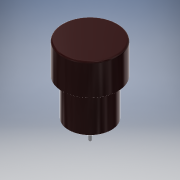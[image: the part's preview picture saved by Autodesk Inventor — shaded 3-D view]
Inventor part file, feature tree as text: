
AUTODESK INVENTOR PART (.ipt)
format: ipt  version: 2019 (Build 230136000, 136)  size: 242,688 bytes
history: native  units: mm
features: fillet x8, extrude x7, sketch x7
ambient origin geometry x8: Origin, YZ Plane, XZ Plane, XY Plane, X Axis, Y Axis, Z Axis, Center Point
bodies: Solid1 (feature_tree)
feature tree (22):
  extrude  "Extrusion1"  Depth=44.0mm TaperAngle=0.0deg
  extrude  "Extrusion2"  Depth=34.0mm TaperAngle=0.0deg
  extrude  "Extrusion3"  Depth=4.0mm TaperAngle=0.0deg
  fillet  "Fillet1"  Radius=2.0mm
  fillet  "Fillet2"  Radius=2.0mm
  fillet  "Fillet4"  Radius=2.0mm
  fillet  "Fillet5"  Radius=0.5mm
  extrude  "Extrusion7"  Depth=3.0mm
  extrude  "Extrusion8"  Depth=3.0mm
  extrude  "Extrusion9"  Depth=2.0mm
  extrude  "Extrusion10"  Depth=0.1mm
  fillet  "Fillet8"  Radius=0.2mm
  fillet  "Fillet9"  Radius=1.0mm
  fillet  "Fillet10"  Radius=0.1mm
  fillet  "Fillet11"  [1 undecoded]
  sketch  "Sketch1"  dims[d0=46.0mm d1=44.0mm d2=0.0mm]
  sketch  "Sketch2"  dims[d3=60.0mm d4=34.0mm d5=0.0mm]
  sketch  "Sketch3"  dims[d6=2.0mm d7=4.0mm d8=0.0mm d9=2.0mm d10=2.0mm d12=2.0mm d13=0.5mm]
  sketch  "Sketch8"  dims[d25=3.0mm d26=0.0mm d27=6.0mm]
  sketch  "Sketch9"  dims[d28=10.0mm d29=0.0mm d30=3.0mm]
  sketch  "Sketch10"  dims[d31=30.0mm d32=0.0mm d33=2.0mm]
  sketch  "Sketch11"  dims[d34=10.0mm d35=0.0mm d36=5.0mm d37=0.2mm d38=1.0mm d39=0.1mm]
note: 1 required parameter value undecoded (feature->parameter linkage not recoverable at this tier; creation-order binding heuristic only, values carry confidence <= 0.55)
